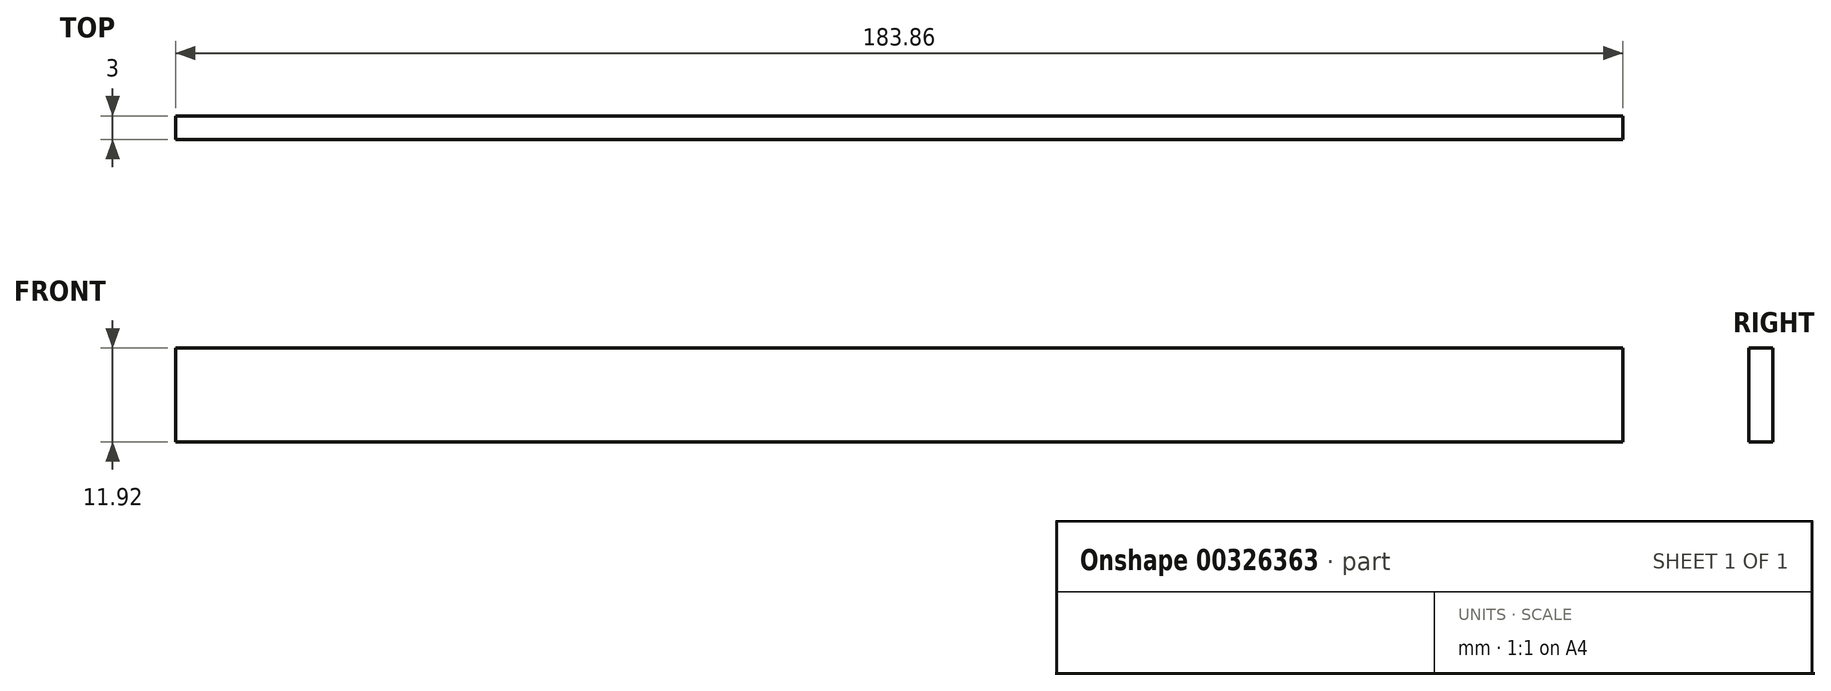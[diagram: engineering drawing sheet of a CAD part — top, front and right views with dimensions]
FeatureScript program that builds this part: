
annotation { "Feature Type Name" : "Feature", "Feature Type Description" : "" }
export const myFeature = defineFeature(function(context is Context, id is Id, definition is map)
    precondition{}
    {
        {
            var Q0;
            Q0=qCreatedBy(makeId("Front.planeOp"),FACE);
            var sketch = newSketch(context, id + "F0", { "sketchPlane" : qUnion([Q0])});
            skLineSegment(sketch, "E0.bottom", {"start": v(-91.92, 0) * mm, "end": v(91.92, 0) * mm});
            skLineSegment(sketch, "E0.top", {"start": v(-91.92, 11.92) * mm, "end": v(91.92, 11.92) * mm});
            skLineSegment(sketch, "E0.left", {"start": v(-91.92, 0) * mm, "end": v(-91.92, 11.92) * mm});
            skLineSegment(sketch, "E0.right", {"start": v(91.92, 0) * mm, "end": v(91.92, 11.92) * mm});
            skSolve(sketch);
        }
        {
            var Q0;
            Q0=makeQuery(id+"F0.imprint","IMPRINT",FACE,{"disambiguationData":[TD([[makeQuery(id+"F0.imprint","IMPRINT",EDGE,{"derivedFrom":sQuery(id+"F0.wireOp",EDGE,"E0.bottom")}),1.0]])]});
            extrude(context, id + "F1", {"entities" : qUnion([Q0]), "depth" : 3 * mm});
        }
    });
